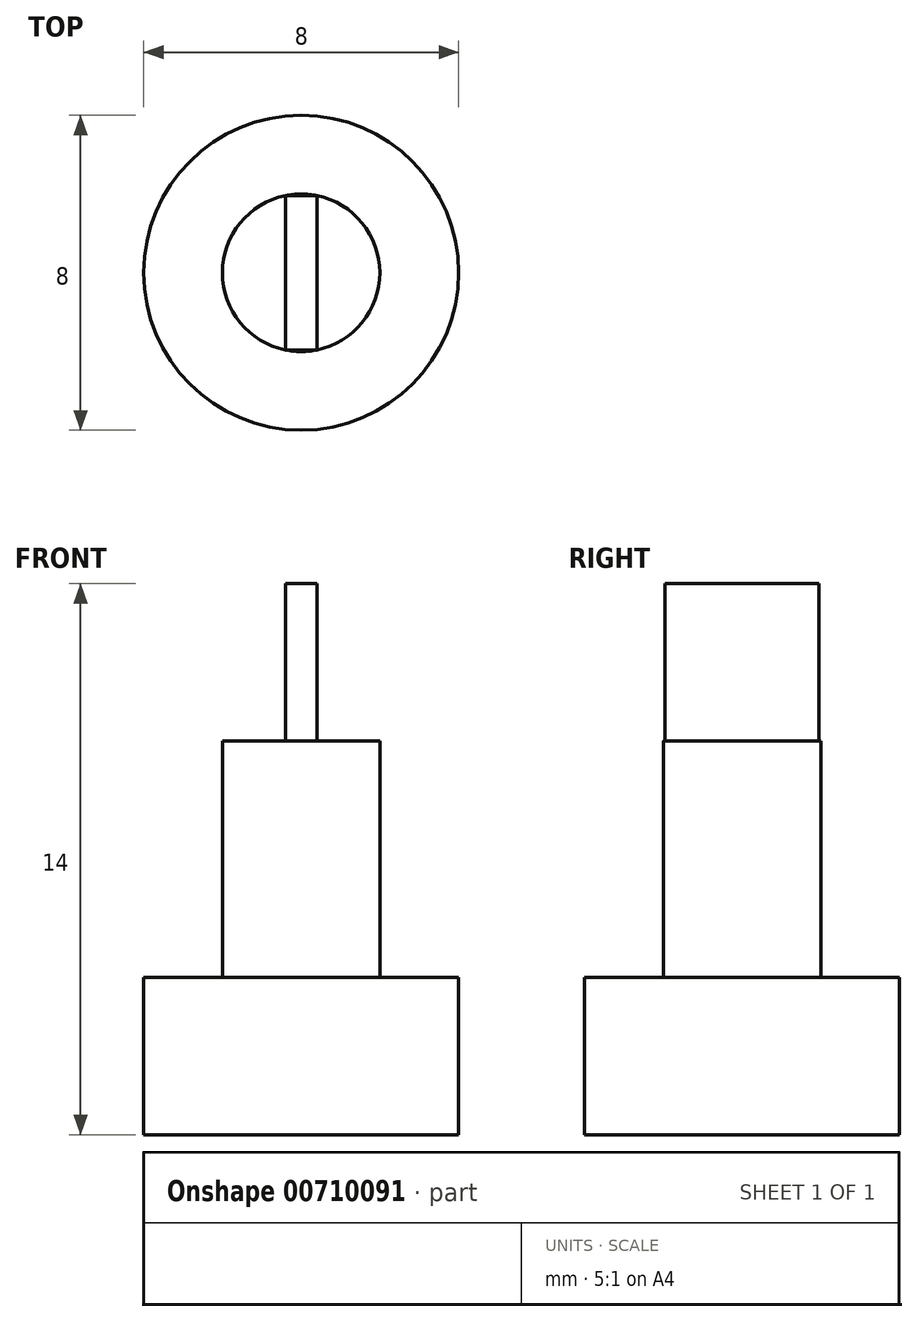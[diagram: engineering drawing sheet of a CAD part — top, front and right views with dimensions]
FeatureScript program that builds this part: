
annotation { "Feature Type Name" : "Feature", "Feature Type Description" : "" }
export const myFeature = defineFeature(function(context is Context, id is Id, definition is map)
    precondition{}
    {
        {
            var Q0;
            Q0=qCreatedBy(makeId("Top.planeOp"),FACE);
            var sketch = newSketch(context, id + "F0", { "sketchPlane" : qUnion([Q0])});
            skCircle(sketch, "E0", {"center": v(-51.7, -21.2) * mm, "radius": 4 * mm});
            skSolve(sketch);
        }
        {
            var Q0;
            Q0=makeQuery(id+"F0.imprint","IMPRINT",FACE,{"disambiguationData":[TD([[makeQuery(id+"F0.imprint","IMPRINT",EDGE,{"derivedFrom":sQuery(id+"F0.wireOp",EDGE,"E0")}),1.0]])]});
            extrude(context, id + "F1", {"entities" : qUnion([Q0]), "depth" : 4 * mm, "offsetDistance" : 25 * mm});
        }
        {
            var Q0;
            Q0=makeQuery(id+"F1.opExtrude","CAP_FACE",FACE,{"disambiguationData":[OSD([sQuery(id+"F0.wireOp",EDGE,"E0")])],"isStart":false});
            var sketch = newSketch(context, id + "F2", { "sketchPlane" : qUnion([Q0])});
            skCircle(sketch, "E1", {"center": v(-51.7, -21.2) * mm, "radius": 2 * mm});
            skSolve(sketch);
        }
        {
            var Q0;
            Q0 = qSketchRegion(id + "F2", true);
            extrude(context, id + "F3", {"entities" : qUnion([Q0]), "operationType" : NewBodyOperationType.ADD, "depth" : 6 * mm, "offsetDistance" : 25 * mm});
        }
        {
            var Q0;
            Q0=makeQuery(id+"F3.opExtrude","CAP_FACE",FACE,{"disambiguationData":[OSD([sQuery(id+"F2.wireOp",EDGE,"E1")])],"isStart":false});
            var sketch = newSketch(context, id + "F4", { "sketchPlane" : qUnion([Q0])});
            skLineSegment(sketch, "E2", {"start": v(-51.3, -23.16) * mm, "end": v(-52.1, -23.16) * mm});
            skLineSegment(sketch, "E3", {"start": v(-52.1, -23.16) * mm, "end": v(-52.1, -19.24) * mm});
            skLineSegment(sketch, "E4", {"start": v(-52.1, -19.24) * mm, "end": v(-51.3, -19.24) * mm});
            skLineSegment(sketch, "E5", {"start": v(-51.3, -19.24) * mm, "end": v(-51.3, -23.16) * mm});
            skSolve(sketch);
        }
        {
            var Q0;
            Q0=makeQuery(id+"F4.imprint","IMPRINT",FACE,{"disambiguationData":[TD([[makeQuery(id+"F4.imprint","IMPRINT",EDGE,{"derivedFrom":sQuery(id+"F4.wireOp",EDGE,"E2")}),-1.0]])]});
            extrude(context, id + "F5", {"entities" : qUnion([Q0]), "operationType" : NewBodyOperationType.ADD, "depth" : 4 * mm, "offsetDistance" : 25 * mm});
        }
    });
